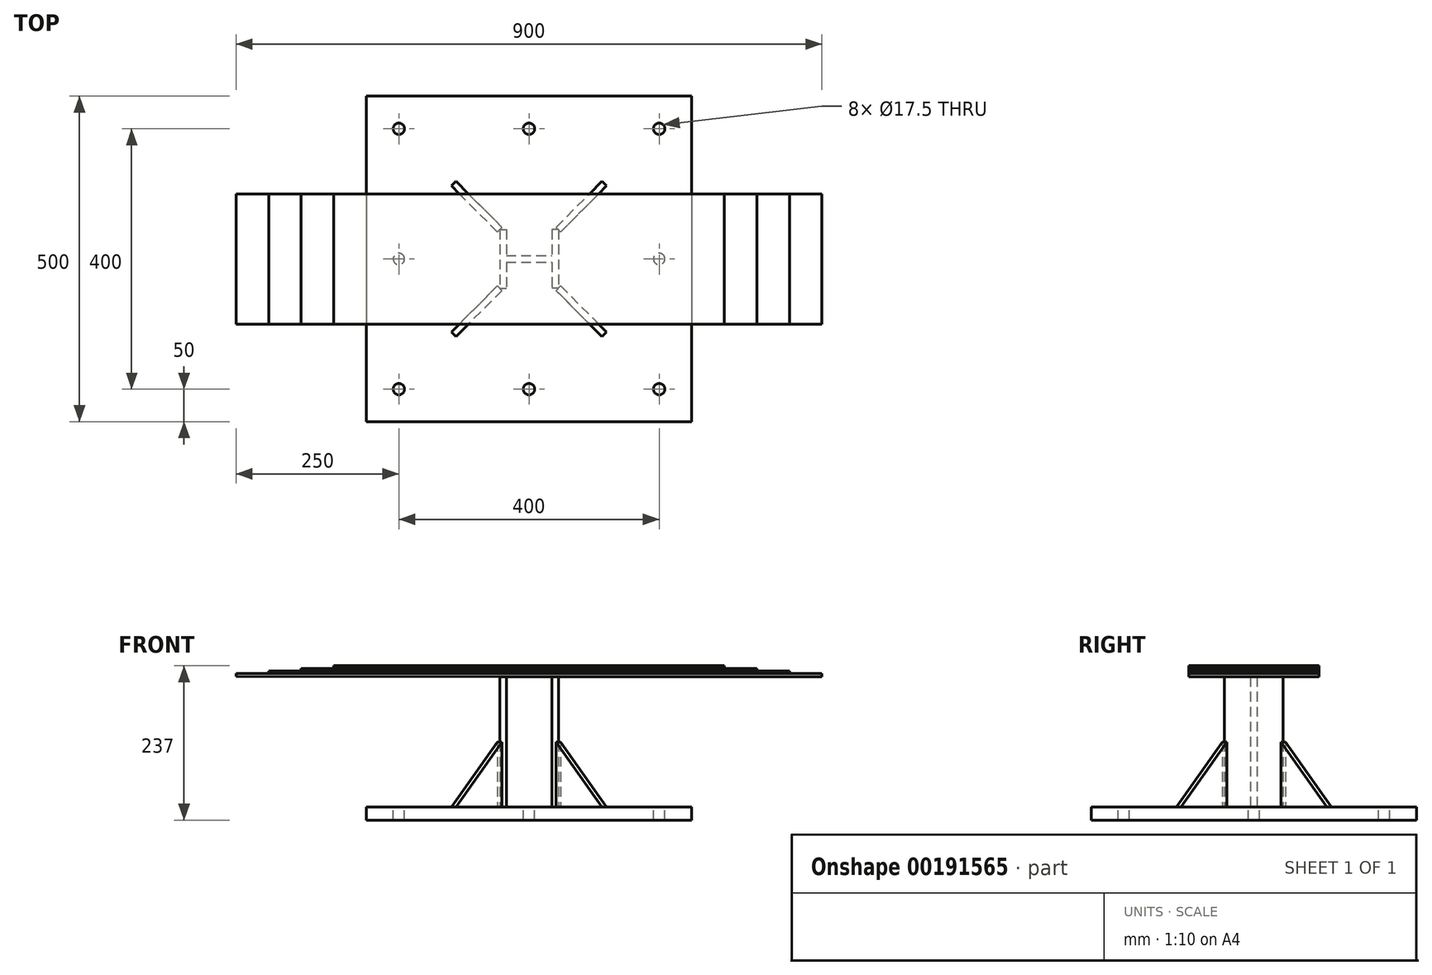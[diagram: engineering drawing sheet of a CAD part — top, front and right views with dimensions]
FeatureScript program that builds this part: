
annotation { "Feature Type Name" : "Feature", "Feature Type Description" : "" }
export const myFeature = defineFeature(function(context is Context, id is Id, definition is map)
    precondition{}
    {
        {
            var Q0;
            Q0=qCreatedBy(makeId("Top.planeOp"),FACE);
            var sketch = newSketch(context, id + "F0", { "sketchPlane" : qUnion([Q0])});
            skLineSegment(sketch, "E0.bottom", {"start": v(-250, 250) * mm, "end": v(250, 250) * mm});
            skLineSegment(sketch, "E0.top", {"start": v(-250, -250) * mm, "end": v(250, -250) * mm});
            skLineSegment(sketch, "E0.left", {"start": v(-250, 250) * mm, "end": v(-250, -250) * mm});
            skLineSegment(sketch, "E0.right", {"start": v(250, 250) * mm, "end": v(250, -250) * mm});
            skPoint(sketch, "E0.middle", {"position": v(0, 0) * mm});
            skSolve(sketch);
        }
        {
            var Q0;
            Q0=makeQuery(id+"F0.imprint","IMPRINT",FACE,{"disambiguationData":[TD([[makeQuery(id+"F0.imprint","IMPRINT",EDGE,{"derivedFrom":sQuery(id+"F0.wireOp",EDGE,"E0.bottom")}),-1.0]])]});
            extrude(context, id + "F1", {"entities" : qUnion([Q0]), "depth" : 20 * mm});
        }
        {
            var Q0;
            Q0=makeQuery(id+"F1.opExtrude","CAP_FACE",FACE,{"disambiguationData":[OSD([sQuery(id+"F0.wireOp",EDGE,"E0.bottom"),sQuery(id+"F0.wireOp",EDGE,"E0.top"),sQuery(id+"F0.wireOp",EDGE,"E0.left"),sQuery(id+"F0.wireOp",EDGE,"E0.right")])],"isStart":false});
            var sketch = newSketch(context, id + "F2", { "sketchPlane" : qUnion([Q0])});
            skLineSegment(sketch, "E1.bottom", {"start": v(-45, 45) * mm, "end": v(45, 45) * mm, "construction": true});
            skLineSegment(sketch, "E1.top", {"start": v(-45, -45) * mm, "end": v(45, -45) * mm, "construction": true});
            skLineSegment(sketch, "E1.left", {"start": v(-45, 45) * mm, "end": v(-45, -45) * mm, "construction": true});
            skLineSegment(sketch, "E1.right", {"start": v(45, 45) * mm, "end": v(45, -45) * mm, "construction": true});
            skPoint(sketch, "E1.middle", {"position": v(0, 0) * mm});
            skSolve(sketch);
        }
        {
            var Q0;
            Q0=makeQuery(id+"F2.imprint","IMPRINT",FACE,{"disambiguationData":[TD([[makeQuery(id+"F2.imprint","IMPRINT",EDGE,{"derivedFrom":makeQuery(id+"F1.opExtrude","CAP_EDGE",EDGE,{"disambiguationData":[OSD([sQuery(id+"F0.wireOp",EDGE,"E0.bottom")])],"isStart":false})}),-1.0]])]});
            var sketch = newSketch(context, id + "F3", { "sketchPlane" : qUnion([Q0])});
            skLineSegment(sketch, "E2.bottom", {"start": v(45, 45) * mm, "end": v(35, 45) * mm});
            skLineSegment(sketch, "E2.top", {"start": v(45, -45) * mm, "end": v(35, -45) * mm});
            skLineSegment(sketch, "E2.left", {"start": v(45, 45) * mm, "end": v(45, -45) * mm});
            skLineSegment(sketch, "E2.right", {"start": v(35, 45) * mm, "end": v(35, 5) * mm});
            skLineSegment(sketch, "E3.bottom", {"start": v(-45, 45) * mm, "end": v(-35, 45) * mm});
            skLineSegment(sketch, "E3.top", {"start": v(-45, -45) * mm, "end": v(-35, -45) * mm});
            skLineSegment(sketch, "E3.left", {"start": v(-45, 45) * mm, "end": v(-45, -45) * mm});
            skLineSegment(sketch, "E3.right", {"start": v(-35, 45) * mm, "end": v(-35, 5) * mm});
            skLineSegment(sketch, "E4.bottom", {"start": v(-35, 5) * mm, "end": v(35, 5) * mm});
            skLineSegment(sketch, "E4.top", {"start": v(-35, -5) * mm, "end": v(35, -5) * mm});
            skPoint(sketch, "E4.middle", {"position": v(0, 0) * mm});
            skLineSegment(sketch, "E5.trimOffspring", {"start": v(35, -5) * mm, "end": v(35, -45) * mm});
            skLineSegment(sketch, "E6.trimOffspring", {"start": v(-35, -5) * mm, "end": v(-35, -45) * mm});
            skSolve(sketch);
        }
        {
            var Q0;
            Q0 = qSketchRegion(id + "F3", true);
            extrude(context, id + "F4", {"entities" : qUnion([Q0]), "operationType" : NewBodyOperationType.ADD, "depth" : 200 * mm});
        }
        {
            var Q0;
            Q0=makeQuery(id+"F4.opExtrude","SWEPT_FACE",FACE,{"disambiguationData":[OSD([sQuery(id+"F3.wireOp",EDGE,"E2.left")])]});
            var sketch = newSketch(context, id + "F5", { "sketchPlane" : qUnion([Q0])});
            skSolve(sketch);
        }
        {
            var Q0;
            Q0=makeQuery(id+"F4.opExtrude","SWEPT_FACE",FACE,{"disambiguationData":[OSD([sQuery(id+"F3.wireOp",EDGE,"E3.left")])]});
            var sketch = newSketch(context, id + "F6", { "sketchPlane" : qUnion([Q0])});
            skSolve(sketch);
        }
        {
            var Q0;
            Q0=makeQuery(id+"F2.imprint","IMPRINT",FACE,{"disambiguationData":[TD([[makeQuery(id+"F2.imprint","IMPRINT",EDGE,{"derivedFrom":makeQuery(id+"F1.opExtrude","CAP_EDGE",EDGE,{"disambiguationData":[OSD([sQuery(id+"F0.wireOp",EDGE,"E0.bottom")])],"isStart":false})}),-1.0]])]});
            var sketch = newSketch(context, id + "F7", { "sketchPlane" : qUnion([Q0])});
            skLineSegment(sketch, "E7", {"start": v(-200, -250) * mm, "end": v(-200, 250) * mm, "construction": true});
            skLineSegment(sketch, "E8", {"start": v(250, 200) * mm, "end": v(-250, 200) * mm, "construction": true});
            skLineSegment(sketch, "E9", {"start": v(200, 250) * mm, "end": v(200, -250) * mm, "construction": true});
            skLineSegment(sketch, "E10", {"start": v(-250, -200) * mm, "end": v(250, -200) * mm, "construction": true});
            skLineSegment(sketch, "E11", {"start": v(-200, 0) * mm, "end": v(200, 0) * mm, "construction": true});
            skLineSegment(sketch, "E12", {"start": v(0, 200) * mm, "end": v(0, -200) * mm, "construction": true});
            skSolve(sketch);
        }
        {
            var Q0;
            Q0=makeQuery(id+"F2.imprint","IMPRINT",FACE,{"disambiguationData":[TD([[makeQuery(id+"F2.imprint","IMPRINT",EDGE,{"derivedFrom":makeQuery(id+"F1.opExtrude","CAP_EDGE",EDGE,{"disambiguationData":[OSD([sQuery(id+"F0.wireOp",EDGE,"E0.bottom")])],"isStart":false})}),-1.0]])]});
            var sketch = newSketch(context, id + "F8", { "sketchPlane" : qUnion([Q0])});
            skPoint(sketch, "E13", {"position": v(-200, 200) * mm});
            skPoint(sketch, "E14", {"position": v(200, 200) * mm});
            skPoint(sketch, "E15", {"position": v(-200, -200) * mm});
            skPoint(sketch, "E16", {"position": v(200, -200) * mm});
            skSolve(sketch);
        }
        {
            var Q0;
            Q0=sQuery(id+"F7.wireOp",VERTEX,"E11.start");
            var Q1;
            Q1=sQuery(id+"F7.wireOp",VERTEX,"E12.end");
            var Q2;
            Q2=sQuery(id+"F7.wireOp",VERTEX,"E11.end");
            var Q3;
            Q3=sQuery(id+"F7.wireOp",VERTEX,"E12.start");
            var Q4;
            Q4=sQuery(id+"F8.wireOp",VERTEX,"E13");
            var Q5;
            Q5=sQuery(id+"F8.wireOp",VERTEX,"E14");
            var Q6;
            Q6=sQuery(id+"F8.wireOp",VERTEX,"E16");
            var Q7;
            Q7=sQuery(id+"F8.wireOp",VERTEX,"E15");
            var Q8;
            Q8=makeQuery(id+"F1.opExtrude","SWEPT_BODY",BODY,{"disambiguationData":[OSD([sQuery(id+"F0.wireOp",EDGE,"E0.bottom"),sQuery(id+"F0.wireOp",EDGE,"E0.top"),sQuery(id+"F0.wireOp",EDGE,"E0.left"),sQuery(id+"F0.wireOp",EDGE,"E0.right")])]});
            hole(context, id + "F9", {"style" : HoleStyle.SIMPLE, "endStyle" : HoleEndStyle.THROUGH, "standardTappedOrClearance" : lookupTablePath({ "standard" : "ISO", "fit" : "Normal", "size" : "M16", "type" : "Clearance" }), "standardBlindInLast" : lookupTablePath({ "fit" : "Standard", "standard" : "ISO", "size" : "M16", "type" : "Clearance" }), "holeDiameter" : 17.5 * mm, "locations" : qUnion([Q0, Q1, Q2, Q3, Q4, Q5, Q6, Q7]), "scope" : qUnion([Q8]), "isTappedThrough" : true});
        }
        {
            var Q0;
            Q0=qCreatedBy(makeId("Front.planeOp"),FACE);
            var sketch = newSketch(context, id + "F10", { "sketchPlane" : qUnion([Q0])});
            skLineSegment(sketch, "E17", {"start": v(0, 220) * mm, "end": v(450, 220) * mm});
            skLineSegment(sketch, "E18", {"start": v(450, 220) * mm, "end": v(450, 225) * mm});
            skLineSegment(sketch, "E19", {"start": v(450, 225) * mm, "end": v(-450, 225) * mm});
            skLineSegment(sketch, "E20", {"start": v(-450, 225) * mm, "end": v(-450, 221) * mm});
            skLineSegment(sketch, "E21", {"start": v(-450, 221) * mm, "end": v(0, 220) * mm});
            skSolve(sketch);
        }
        {
            var Q0;
            Q0=makeQuery(id+"F10.imprint","IMPRINT",FACE,{"disambiguationData":[TD([[makeQuery(id+"F10.imprint","IMPRINT",EDGE,{"derivedFrom":sQuery(id+"F10.wireOp",EDGE,"E17")}),1.0]])]});
            extrude(context, id + "F11", {"entities" : qUnion([Q0]), "depth" : 100 * mm, "hasSecondDirection" : true, "secondDirectionOppositeDirection" : true, "secondDirectionDepth" : 100 * mm});
        }
        {
            var Q0;
            Q0=qCreatedBy(makeId("Front.planeOp"),FACE);
            var sketch = newSketch(context, id + "F12", { "sketchPlane" : qUnion([Q0])});
            skLineSegment(sketch, "E22.bottom", {"start": v(-400, 225) * mm, "end": v(400, 225) * mm});
            skLineSegment(sketch, "E22.top", {"start": v(-400, 229) * mm, "end": v(400, 229) * mm});
            skLineSegment(sketch, "E22.left", {"start": v(-400, 225) * mm, "end": v(-400, 229) * mm});
            skLineSegment(sketch, "E22.right", {"start": v(400, 225) * mm, "end": v(400, 229) * mm});
            skSolve(sketch);
        }
        {
            var Q0;
            Q0=makeQuery(id+"F12.imprint","IMPRINT",FACE,{"disambiguationData":[TD([[makeQuery(id+"F12.imprint","IMPRINT",EDGE,{"derivedFrom":sQuery(id+"F12.wireOp",EDGE,"E22.bottom")}),1.0]])]});
            extrude(context, id + "F13", {"entities" : qUnion([Q0]), "depth" : 100 * mm, "hasSecondDirection" : true, "secondDirectionOppositeDirection" : true, "secondDirectionDepth" : 100 * mm});
        }
        {
            var Q0;
            Q0=qCreatedBy(makeId("Front.planeOp"),FACE);
            var sketch = newSketch(context, id + "F14", { "sketchPlane" : qUnion([Q0])});
            skLineSegment(sketch, "E23", {"start": v(0, 229) * mm, "end": v(350, 229) * mm});
            skLineSegment(sketch, "E24", {"start": v(350, 229) * mm, "end": v(350, 233) * mm});
            skLineSegment(sketch, "E25", {"start": v(350, 233) * mm, "end": v(-350, 233) * mm});
            skLineSegment(sketch, "E26", {"start": v(-350, 233) * mm, "end": v(-350, 229) * mm});
            skLineSegment(sketch, "E27", {"start": v(-350, 229) * mm, "end": v(0, 229) * mm});
            skSolve(sketch);
        }
        {
            var Q0;
            Q0 = qSketchRegion(id + "F14", true);
            extrude(context, id + "F15", {"entities" : qUnion([Q0]), "depth" : 100 * mm, "hasSecondDirection" : true, "secondDirectionOppositeDirection" : true, "secondDirectionDepth" : 100 * mm});
        }
        {
            var Q0;
            Q0=qCreatedBy(makeId("Front.planeOp"),FACE);
            var sketch = newSketch(context, id + "F16", { "sketchPlane" : qUnion([Q0])});
            skLineSegment(sketch, "E28.bottom", {"start": v(-300, 233) * mm, "end": v(300, 233) * mm});
            skLineSegment(sketch, "E28.top", {"start": v(-300, 237) * mm, "end": v(300, 237) * mm});
            skLineSegment(sketch, "E28.left", {"start": v(-300, 233) * mm, "end": v(-300, 237) * mm});
            skLineSegment(sketch, "E28.right", {"start": v(300, 233) * mm, "end": v(300, 237) * mm});
            skSolve(sketch);
        }
        {
            var Q0;
            Q0=makeQuery(id+"F16.imprint","IMPRINT",FACE,{"disambiguationData":[TD([[makeQuery(id+"F16.imprint","IMPRINT",EDGE,{"derivedFrom":sQuery(id+"F16.wireOp",EDGE,"E28.bottom")}),1.0]])]});
            extrude(context, id + "F17", {"entities" : qUnion([Q0]), "depth" : 100 * mm, "hasSecondDirection" : true, "secondDirectionOppositeDirection" : true, "secondDirectionDepth" : 100 * mm});
        }
        {
            var Q0;
            Q0=makeQuery(id+"F2.imprint","IMPRINT",FACE,{"disambiguationData":[TD([[makeQuery(id+"F2.imprint","IMPRINT",EDGE,{"derivedFrom":makeQuery(id+"F1.opExtrude","CAP_EDGE",EDGE,{"disambiguationData":[OSD([sQuery(id+"F0.wireOp",EDGE,"E0.bottom")])],"isStart":false})}),-1.0]])]});
            var sketch = newSketch(context, id + "F18", { "sketchPlane" : qUnion([Q0])});
            skLineSegment(sketch, "E29", {"start": v(-250, 250) * mm, "end": v(250, -250) * mm, "construction": true});
            skLineSegment(sketch, "E30", {"start": v(-250, -250) * mm, "end": v(250, 250) * mm, "construction": true});
            skLineSegment(sketch, "E31", {"start": v(41.46, 48.54) * mm, "end": v(48.54, 41.46) * mm});
            skLineSegment(sketch, "E32", {"start": v(41.46, 48.54) * mm, "end": v(112.18, 119.25) * mm});
            skLineSegment(sketch, "E33", {"start": v(112.18, 119.25) * mm, "end": v(119.25, 112.18) * mm});
            skLineSegment(sketch, "E34", {"start": v(119.25, 112.18) * mm, "end": v(48.54, 41.46) * mm});
            skPoint(sketch, "E35.center", {"position": v(0, 0) * mm});
            skSolve(sketch);
        }
        {
            var Q0;
            Q0 = qSketchRegion(id + "F18", true);
            extrude(context, id + "F19", {"entities" : qUnion([Q0]), "depth" : 100 * mm});
        }
        {
            var Q0;
            Q0=makeQuery(id+"F19.opExtrude","SWEPT_FACE",FACE,{"disambiguationData":[OSD([sQuery(id+"F18.wireOp",EDGE,"E32")])]});
            var sketch = newSketch(context, id + "F20", { "sketchPlane" : qUnion([Q0])});
            skLineSegment(sketch, "E36", {"start": v(-63.64, 120) * mm, "end": v(-163.64, 20) * mm});
            skLineSegment(sketch, "E37", {"start": v(-3.2, -5.27) * mm, "end": v(-3.2, 234.74) * mm, "construction": true});
            skSolve(sketch);
        }
        {
            var Q0;
            Q0 = qSketchRegion(id + "F20", true);
            var Q1;
            Q1=makeQuery(id+"F20.imprint","IMPRINT",FACE,{"disambiguationData":[TD([[makeQuery(id+"F20.imprint","IMPRINT",EDGE,{"derivedFrom":sQuery(id+"F20.wireOp",EDGE,"E36")}),-1.0]])]});
            extrude(context, id + "F21", {"entities" : qUnion([Q0, Q1]), "operationType" : NewBodyOperationType.REMOVE, "oppositeDirection" : true, "depth" : 10 * mm});
        }
        {
            var Q0;
            Q0=qCreatedBy(makeId("Front.planeOp"),FACE);
            var sketch = newSketch(context, id + "F22", { "sketchPlane" : qUnion([Q0])});
            skLineSegment(sketch, "E38", {"start": v(0, 0) * mm, "end": v(0, 280.54) * mm, "construction": true});
            skSolve(sketch);
        }
        {
            var Q0;
            Q0=makeQuery(id+"F19.opExtrude","SWEPT_BODY",BODY,{"disambiguationData":[OSD([sQuery(id+"F18.wireOp",EDGE,"E31"),sQuery(id+"F18.wireOp",EDGE,"E32"),sQuery(id+"F18.wireOp",EDGE,"E33"),sQuery(id+"F18.wireOp",EDGE,"E34")])]});
            var Q1;
            Q1=sQuery(id+"F22.wireOp",EDGE,"E38");
            circularPattern(context, id + "F23", {"entities" : qUnion([Q0]), "axis" : qUnion([Q1]), "angle" : 360 * degree, "instanceCount" : 4, "equalSpace" : true});
        }
    });
